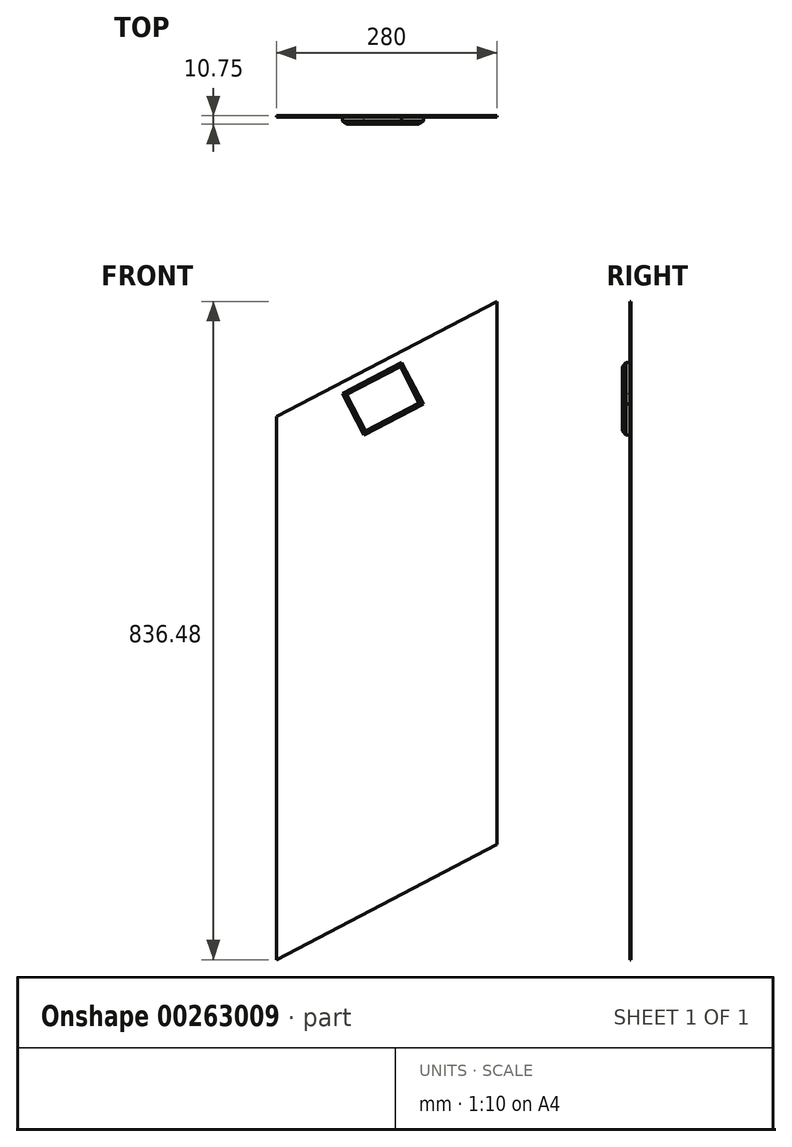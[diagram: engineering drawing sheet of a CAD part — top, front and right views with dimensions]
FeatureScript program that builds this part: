
annotation { "Feature Type Name" : "Feature", "Feature Type Description" : "" }
export const myFeature = defineFeature(function(context is Context, id is Id, definition is map)
    precondition{}
    {
        {
            var Q0;
            Q0=qCreatedBy(makeId("Front.planeOp"),FACE);
            var sketch = newSketch(context, id + "F0", { "sketchPlane" : qUnion([Q0])});
            skLineSegment(sketch, "E0", {"start": v(-280, 543.52) * mm, "end": v(-280, -146.48) * mm});
            skLineSegment(sketch, "E1", {"start": v(-280, -146.48) * mm, "end": v(0, 0) * mm});
            skLineSegment(sketch, "E2", {"start": v(-280, 543.52) * mm, "end": v(0, 690) * mm});
            skLineSegment(sketch, "E3", {"start": v(0, 0) * mm, "end": v(0, 690) * mm});
            skSolve(sketch);
        }
        {
            var Q0;
            Q0 = qSketchRegion(id + "F0", true);
            extrude(context, id + "F1", {"entities" : qUnion([Q0]), "depth" : 1.75 * mm});
        }
        {
            var Q0;
            Q0=makeQuery(id+"F1.opExtrude","CAP_FACE",FACE,{"disambiguationData":[OSD([sQuery(id+"F0.wireOp",EDGE,"E0"),sQuery(id+"F0.wireOp",EDGE,"E1"),sQuery(id+"F0.wireOp",EDGE,"E2"),sQuery(id+"F0.wireOp",EDGE,"E3")])],"isStart":false});
            var sketch = newSketch(context, id + "F2", { "sketchPlane" : qUnion([Q0])});
            skLineSegment(sketch, "E4", {"start": v(-196.17, 573.04) * mm, "end": v(-120.85, 612.45) * mm});
            skLineSegment(sketch, "E5", {"start": v(-120.85, 612.45) * mm, "end": v(-93.04, 559.28) * mm});
            skLineSegment(sketch, "E6", {"start": v(-93.04, 559.28) * mm, "end": v(-168.35, 519.88) * mm});
            skLineSegment(sketch, "E7", {"start": v(-168.35, 519.88) * mm, "end": v(-196.17, 573.04) * mm});
            skLineSegment(sketch, "E8", {"start": v(-93.04, 559.28) * mm, "end": v(0, 607.95) * mm, "construction": true});
            skSolve(sketch);
        }
        {
            var Q0;
            Q0 = qSketchRegion(id + "F2", true);
            extrude(context, id + "F3", {"entities" : qUnion([Q0]), "operationType" : NewBodyOperationType.ADD, "depth" : 9 * mm});
        }
        {
            var Q0;
            Q0=makeQuery(id+"F3.opExtrude","CAP_FACE",FACE,{"disambiguationData":[OSD([sQuery(id+"F2.wireOp",EDGE,"E4"),sQuery(id+"F2.wireOp",EDGE,"E5"),sQuery(id+"F2.wireOp",EDGE,"E6"),sQuery(id+"F2.wireOp",EDGE,"E7")])],"isStart":false});
            chamfer(context, id + "F4", {"entities" : qUnion([Q0]), "width" : 4 * mm, "tangentPropagation" : true});
        }
    });
